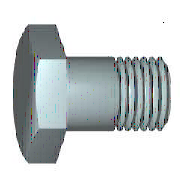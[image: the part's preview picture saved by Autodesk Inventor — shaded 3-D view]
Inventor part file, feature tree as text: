
AUTODESK INVENTOR PART (.ipt)
format: ipt  version: 2022 (Build 260153000, 153)  size: 196,608 bytes
history: native  units: mm (DEFAULTED — no unit token found)
features: sketch x3, other x1, extrude x1, chamfer x1, plane x1
ambient origin geometry x7: Origin, YZ Plane, XZ Plane, X Axis, Y Axis, Z Axis, Center Point
bodies: Solid1 (feature_tree)
feature tree (7):
  other  "Cuerpo"
  extrude  "Cabeza"  Depth=13.6mm
  chamfer  "Chaflán1"  Distance=3.0mm
  plane  "Work Plane1"
  sketch  "Boceto1"  dims[d0=16.0mm d1=13.6mm]
  sketch  "Boceto2"  dims[d2=5.0mm]
  sketch  "Boceto4"  dims[d12=90.0deg d3=3.0mm d4=0.0mm d5=30.0deg d21=90.0deg d6=0.49076mm d7=0.49086mm d8=0.0mm d9=0.5001mm d10=8.0mm d11=8.0mm d13=0.49086mm d14=5.0mm d15=13.6mm d16=0.0mm d19=8.0mm d55=45.0deg d57=0.0mm d58=0.0mm]
